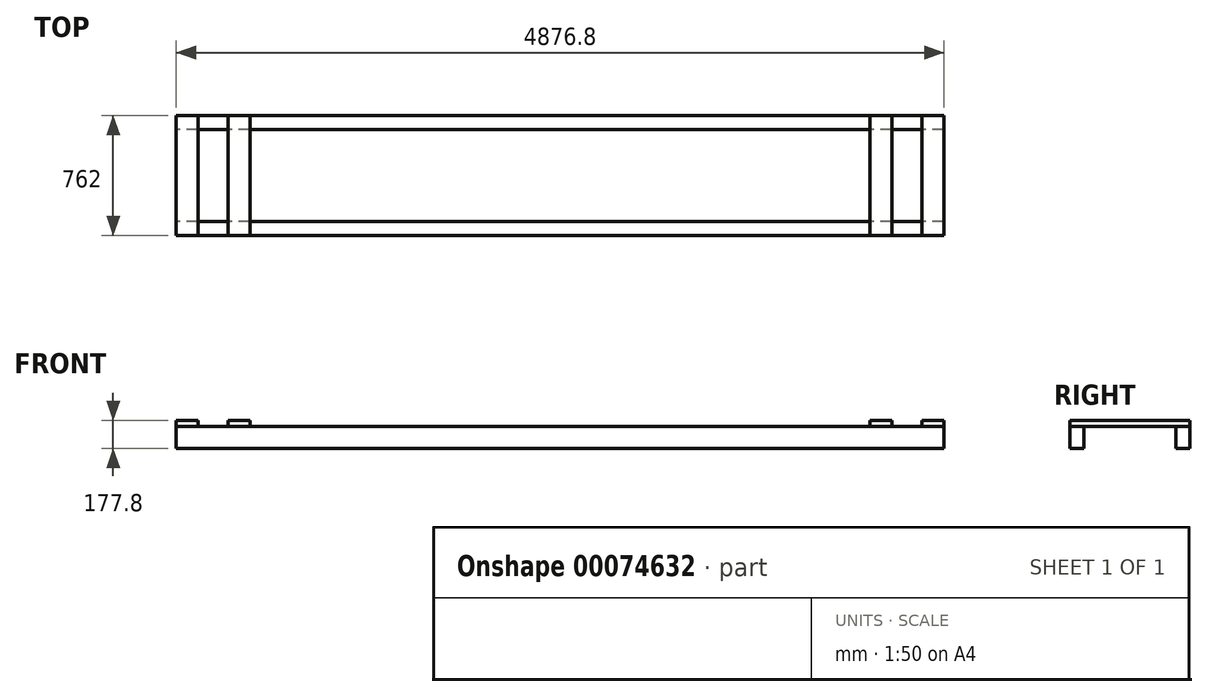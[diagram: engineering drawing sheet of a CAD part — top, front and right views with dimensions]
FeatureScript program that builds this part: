
annotation { "Feature Type Name" : "Feature", "Feature Type Description" : "" }
export const myFeature = defineFeature(function(context is Context, id is Id, definition is map)
    precondition{}
    {
        {
            var Q0;
            Q0=qCreatedBy(makeId("Right.planeOp"),FACE);
            var sketch = newSketch(context, id + "F0", { "sketchPlane" : qUnion([Q0])});
            skLineSegment(sketch, "E0.bottom", {"start": v(-292.1, 0) * mm, "end": v(-381, 0) * mm});
            skLineSegment(sketch, "E0.top", {"start": v(-292.1, 139.7) * mm, "end": v(-381, 139.7) * mm});
            skLineSegment(sketch, "E0.left", {"start": v(-292.1, 0) * mm, "end": v(-292.1, 139.7) * mm});
            skLineSegment(sketch, "E0.right", {"start": v(-381, 0) * mm, "end": v(-381, 139.7) * mm});
            skLineSegment(sketch, "E1.bottom", {"start": v(292.1, 0) * mm, "end": v(381, 0) * mm});
            skLineSegment(sketch, "E1.top", {"start": v(292.1, 139.7) * mm, "end": v(381, 139.7) * mm});
            skLineSegment(sketch, "E1.left", {"start": v(292.1, 0) * mm, "end": v(292.1, 139.7) * mm});
            skLineSegment(sketch, "E1.right", {"start": v(381, 0) * mm, "end": v(381, 139.7) * mm});
            skSolve(sketch);
        }
        {
            var Q0;
            Q0 = qSketchRegion(id + "F0", true);
            extrude(context, id + "F1", {"entities" : qUnion([Q0]), "endBound" : BoundingType.SYMMETRIC, "depth" : 4876.8 * mm});
        }
        {
            var Q0;
            Q0=makeQuery(id+"F1.opExtrude","SWEPT_FACE",FACE,{"disambiguationData":[OSD([sQuery(id+"F0.wireOp",EDGE,"E0.right")])]});
            var sketch = newSketch(context, id + "F2", { "sketchPlane" : qUnion([Q0])});
            skLineSegment(sketch, "E2.bottom", {"start": v(2438.4, 139.7) * mm, "end": v(2298.7, 139.7) * mm});
            skLineSegment(sketch, "E2.top", {"start": v(2438.4, 177.8) * mm, "end": v(2298.7, 177.8) * mm});
            skLineSegment(sketch, "E2.left", {"start": v(2438.4, 139.7) * mm, "end": v(2438.4, 177.8) * mm});
            skLineSegment(sketch, "E2.right", {"start": v(2298.7, 139.7) * mm, "end": v(2298.7, 177.8) * mm});
            skLineSegment(sketch, "E3.bottom", {"start": v(2108.2, 139.7) * mm, "end": v(1968.5, 139.7) * mm});
            skLineSegment(sketch, "E3.top", {"start": v(2108.2, 177.8) * mm, "end": v(1968.5, 177.8) * mm});
            skLineSegment(sketch, "E3.left", {"start": v(2108.2, 139.7) * mm, "end": v(2108.2, 177.8) * mm});
            skLineSegment(sketch, "E3.right", {"start": v(1968.5, 139.7) * mm, "end": v(1968.5, 177.8) * mm});
            skSolve(sketch);
        }
        {
            var Q0;
            Q0 = qSketchRegion(id + "F2", true);
            extrude(context, id + "F3", {"entities" : qUnion([Q0]), "oppositeDirection" : true, "depth" : 762 * mm});
        }
        {
            var Q0;
            Q0=makeQuery(id+"F3.opExtrude","SWEPT_BODY",BODY,{"disambiguationData":[OSD([sQuery(id+"F2.wireOp",EDGE,"E2.bottom"),sQuery(id+"F2.wireOp",EDGE,"E2.top"),sQuery(id+"F2.wireOp",EDGE,"E2.left"),sQuery(id+"F2.wireOp",EDGE,"E2.right")])]});
            var Q1;
            Q1=makeQuery(id+"F3.opExtrude","SWEPT_BODY",BODY,{"disambiguationData":[OSD([sQuery(id+"F2.wireOp",EDGE,"E3.bottom"),sQuery(id+"F2.wireOp",EDGE,"E3.top"),sQuery(id+"F2.wireOp",EDGE,"E3.left"),sQuery(id+"F2.wireOp",EDGE,"E3.right")])]});
            var Q2;
            Q2=qCreatedBy(makeId("Right.planeOp"),FACE);
            mirror(context, id + "F4", {"entities" : qUnion([Q0, Q1]), "mirrorPlane" : qUnion([Q2])});
        }
    });
